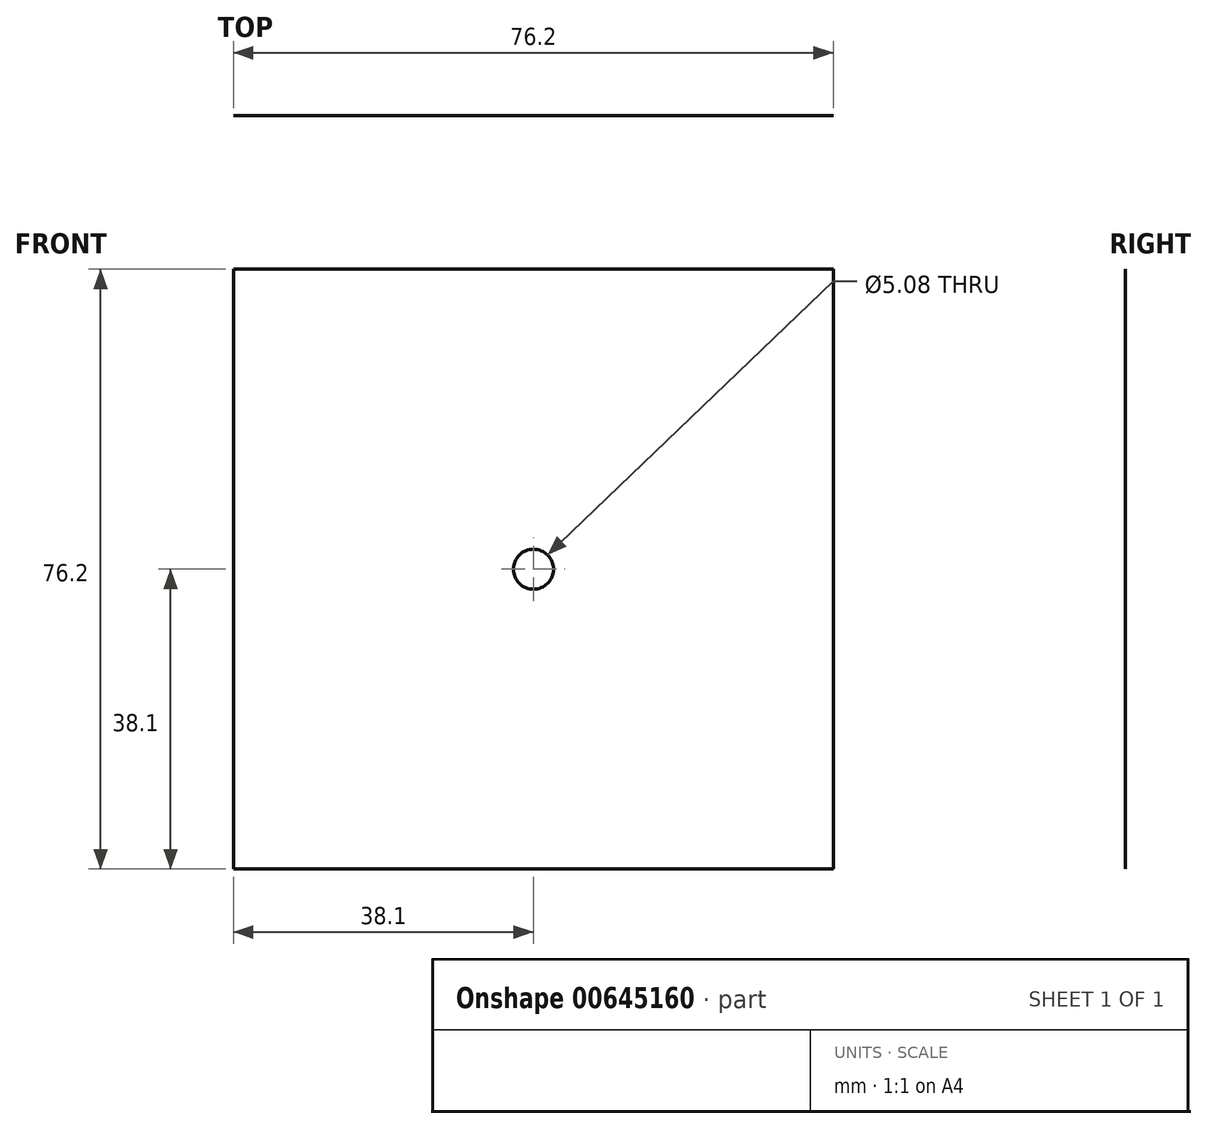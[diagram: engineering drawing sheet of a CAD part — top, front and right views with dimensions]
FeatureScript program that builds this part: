
annotation { "Feature Type Name" : "Feature", "Feature Type Description" : "" }
export const myFeature = defineFeature(function(context is Context, id is Id, definition is map)
    precondition{}
    {
        {
            var Q0;
            Q0=qCreatedBy(makeId("Front.planeOp"),FACE);
            var sketch = newSketch(context, id + "F0", { "sketchPlane" : qUnion([Q0])});
            skLineSegment(sketch, "E0.bottom", {"start": v(38.1, 38.1) * mm, "end": v(-38.1, 38.1) * mm});
            skLineSegment(sketch, "E0.top", {"start": v(38.1, -38.1) * mm, "end": v(-38.1, -38.1) * mm});
            skLineSegment(sketch, "E0.left", {"start": v(38.1, 38.1) * mm, "end": v(38.1, -38.1) * mm});
            skLineSegment(sketch, "E0.right", {"start": v(-38.1, 38.1) * mm, "end": v(-38.1, -38.1) * mm});
            skPoint(sketch, "E0.middle", {"position": v(0, 0) * mm});
            skSolve(sketch);
        }
        {
            var Q0;
            Q0=makeQuery(id+"F0.imprint","IMPRINT",FACE,{"disambiguationData":[TD([[makeQuery(id+"F0.imprint","IMPRINT",EDGE,{"derivedFrom":sQuery(id+"F0.wireOp",EDGE,"E0.bottom")}),1.0]])]});
            extrude(context, id + "F1", {"entities" : qUnion([Q0]), "depth" : 1 / 406.4 * mm, "offsetDistance" : 25.4 * mm});
        }
        {
            var Q0;
            Q0=makeQuery(id+"F1.opExtrude","CAP_FACE",FACE,{"disambiguationData":[OSD([sQuery(id+"F0.wireOp",EDGE,"E0.bottom"),sQuery(id+"F0.wireOp",EDGE,"E0.top"),sQuery(id+"F0.wireOp",EDGE,"E0.left"),sQuery(id+"F0.wireOp",EDGE,"E0.right")])],"isStart":false});
            var sketch = newSketch(context, id + "F2", { "sketchPlane" : qUnion([Q0])});
            skCircle(sketch, "E1", {"center": v(0, 0) * mm, "radius": 2.54 * mm});
            skSolve(sketch);
        }
        {
            var Q0;
            Q0=makeQuery(id+"F2.imprint","IMPRINT",FACE,{"disambiguationData":[TD([[makeQuery(id+"F2.imprint","IMPRINT",EDGE,{"derivedFrom":sQuery(id+"F2.wireOp",EDGE,"E1")}),1.0]])]});
            var Q1;
            Q1=sQuery(id+"F2.wireOp",EDGE,"E1");
            extrude(context, id + "F3", {"entities" : qUnion([Q0]), "operationType" : NewBodyOperationType.REMOVE, "surfaceEntities" : qUnion([Q1]), "oppositeDirection" : true, "depth" : 25.4 * mm, "offsetDistance" : 25.4 * mm});
        }
    });
